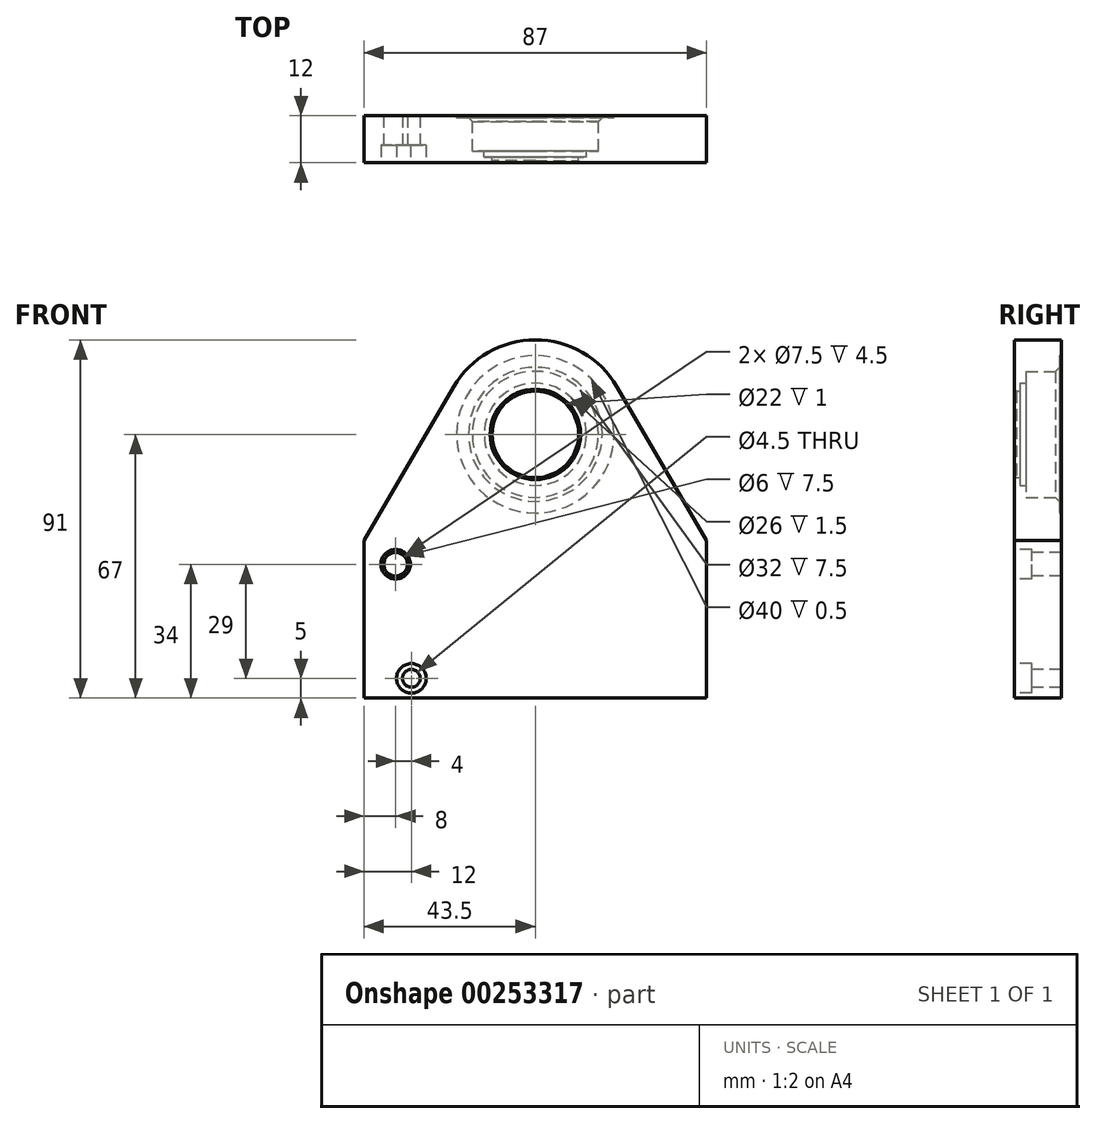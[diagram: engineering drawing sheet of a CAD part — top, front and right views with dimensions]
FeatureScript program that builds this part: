
annotation { "Feature Type Name" : "Feature", "Feature Type Description" : "" }
export const myFeature = defineFeature(function(context is Context, id is Id, definition is map)
    precondition{}
    {
        {
            var Q0;
            Q0=qCreatedBy(makeId("Front.planeOp"),FACE);
            var sketch = newSketch(context, id + "F0", { "sketchPlane" : qUnion([Q0])});
            skLineSegment(sketch, "E0.bottom", {"start": v(-43.5, 0) * mm, "end": v(43.5, 0) * mm});
            skLineSegment(sketch, "E0.left", {"start": v(-43.5, 0) * mm, "end": v(-43.5, 40) * mm});
            skLineSegment(sketch, "E0.right", {"start": v(43.5, 0) * mm, "end": v(43.5, 40) * mm});
            skCircle(sketch, "E1", {"center": v(0, 67) * mm, "radius": 11 * mm});
            skLineSegment(sketch, "E2", {"start": v(-43.5, 40) * mm, "end": v(-20.74, 79.08) * mm});
            skLineSegment(sketch, "E3", {"start": v(43.5, 40) * mm, "end": v(20.74, 79.08) * mm});
            skArc(sketch, "E4", {"start": v(-20.74, 79.08) * mm, "mid": v(0, 91) * mm, "end": v(20.74, 79.08) * mm});
            skCircle(sketch, "E5", {"center": v(-35.5, 34) * mm, "radius": 3 * mm, "construction": true});
            skCircle(sketch, "E6", {"center": v(-35.5, 34) * mm, "radius": 3.75 * mm, "construction": true});
            skCircle(sketch, "E7.MirrorC", {"center": v(35.5, 34) * mm, "radius": 3.75 * mm, "construction": true});
            skCircle(sketch, "E8.MirrorC", {"center": v(35.5, 34) * mm, "radius": 3 * mm, "construction": true});
            skCircle(sketch, "E9", {"center": v(-31.5, 5) * mm, "radius": 2.25 * mm, "construction": true});
            skCircle(sketch, "E10", {"center": v(-31.5, 5) * mm, "radius": 3.75 * mm, "construction": true});
            skCircle(sketch, "E11.MirrorC", {"center": v(31.5, 5) * mm, "radius": 2.25 * mm, "construction": true});
            skCircle(sketch, "E12.MirrorC", {"center": v(31.5, 5) * mm, "radius": 3.75 * mm, "construction": true});
            skSolve(sketch);
        }
        {
            var Q0;
            Q0=makeQuery(id+"F0.imprint","IMPRINT",FACE,{"disambiguationData":[TD([[makeQuery(id+"F0.imprint","IMPRINT",EDGE,{"derivedFrom":sQuery(id+"F0.wireOp",EDGE,"E0.bottom")}),1.0]])]});
            extrude(context, id + "F1", {"entities" : qUnion([Q0]), "depth" : 12 * mm});
        }
        {
            var Q0;
            Q0=makeQuery(id+"F1.opExtrude","CAP_FACE",FACE,{"disambiguationData":[OSD([sQuery(id+"F0.wireOp",EDGE,"E0.bottom"),sQuery(id+"F0.wireOp",EDGE,"E0.left"),sQuery(id+"F0.wireOp",EDGE,"E0.right"),sQuery(id+"F0.wireOp",EDGE,"E1"),sQuery(id+"F0.wireOp",EDGE,"E2"),sQuery(id+"F0.wireOp",EDGE,"E3"),sQuery(id+"F0.wireOp",EDGE,"E4")])],"isStart":false});
            var sketch = newSketch(context, id + "F2", { "sketchPlane" : qUnion([Q0])});
            skCircle(sketch, "E13.0", {"center": v(-35.5, 34) * mm, "radius": 3.75 * mm});
            skCircle(sketch, "E14.0", {"center": v(-35.5, 34) * mm, "radius": 3 * mm});
            skCircle(sketch, "E15.0", {"center": v(-31.5, 5) * mm, "radius": 3.75 * mm});
            skCircle(sketch, "E16.0", {"center": v(-31.5, 5) * mm, "radius": 2.25 * mm});
            skSolve(sketch);
        }
        {
            var Q0;
            Q0=makeQuery(id+"F2.imprint","IMPRINT",FACE,{"disambiguationData":[TD([[makeQuery(id+"F2.imprint","IMPRINT",EDGE,{"derivedFrom":sQuery(id+"F2.wireOp",EDGE,"E14.0")}),1.0]])]});
            extrude(context, id + "F3", {"entities" : qUnion([Q0]), "operationType" : NewBodyOperationType.REMOVE, "oppositeDirection" : true, "depth" : 18 * mm});
        }
        {
            var Q0;
            Q0=makeQuery(id+"F2.imprint","IMPRINT",FACE,{"disambiguationData":[TD([[makeQuery(id+"F2.imprint","IMPRINT",EDGE,{"derivedFrom":sQuery(id+"F2.wireOp",EDGE,"E13.0")}),1.0]])]});
            extrude(context, id + "F4", {"entities" : qUnion([Q0]), "operationType" : NewBodyOperationType.REMOVE, "oppositeDirection" : true, "depth" : 4.5 * mm});
        }
        {
            var Q0;
            Q0=makeQuery(id+"F2.imprint","IMPRINT",FACE,{"disambiguationData":[TD([[makeQuery(id+"F2.imprint","IMPRINT",EDGE,{"derivedFrom":sQuery(id+"F2.wireOp",EDGE,"E16.0")}),1.0]])]});
            extrude(context, id + "F5", {"entities" : qUnion([Q0]), "operationType" : NewBodyOperationType.REMOVE, "endBound" : BoundingType.THROUGH_ALL, "oppositeDirection" : true, "depth" : 25 * mm});
        }
        {
            var Q0;
            Q0=makeQuery(id+"F2.imprint","IMPRINT",FACE,{"disambiguationData":[TD([[makeQuery(id+"F2.imprint","IMPRINT",EDGE,{"derivedFrom":sQuery(id+"F2.wireOp",EDGE,"E15.0")}),1.0]])]});
            extrude(context, id + "F6", {"entities" : qUnion([Q0]), "operationType" : NewBodyOperationType.REMOVE, "oppositeDirection" : true, "depth" : 4.5 * mm});
        }
        {
            var Q0;
            Q0=qCreatedBy(makeId("Top.planeOp"),FACE);
            cPlane(context, id + "F7", {"entities" : qUnion([Q0]), "cplaneType" : CPlaneType.OFFSET, "offset" : 67 * mm, "width" : 150 * mm, "height" : 150 * mm});
        }
        {
            var Q0;
            Q0=qCreatedBy(id+"F7.planeOp",FACE);
            var sketch = newSketch(context, id + "F8", { "sketchPlane" : qUnion([Q0])});
            skLineSegment(sketch, "E17.0", {"start": v(-11, -12) * mm, "end": v(11, -12) * mm});
            skLineSegment(sketch, "E18.0", {"start": v(-20, 0) * mm, "end": v(20, 0) * mm});
            skLineSegment(sketch, "E19.0", {"start": v(11, -12) * mm, "end": v(-11, -12) * mm});
            skLineSegment(sketch, "E20", {"start": v(11, -12) * mm, "end": v(11, -10.5) * mm});
            skLineSegment(sketch, "E21", {"start": v(11, -10.5) * mm, "end": v(13, -10.5) * mm});
            skLineSegment(sketch, "E22", {"start": v(13, -10.5) * mm, "end": v(13, -9) * mm});
            skLineSegment(sketch, "E23", {"start": v(13, -9) * mm, "end": v(16, -9) * mm});
            skLineSegment(sketch, "E24", {"start": v(16, -9) * mm, "end": v(16, -1.5) * mm});
            skLineSegment(sketch, "E25", {"start": v(17, -0.5) * mm, "end": v(20, -0.5) * mm});
            skLineSegment(sketch, "E26", {"start": v(20, -0.5) * mm, "end": v(20, 0) * mm});
            skLineSegment(sketch, "E27", {"start": v(16, -1.5) * mm, "end": v(17, -0.5) * mm});
            skLineSegment(sketch, "E28.MirrorCS", {"start": v(-11, -12) * mm, "end": v(-11, -10.5) * mm, "construction": true});
            skLineSegment(sketch, "E29.MirrorCS", {"start": v(-13, -10.5) * mm, "end": v(-13, -9) * mm, "construction": true});
            skLineSegment(sketch, "E30.MirrorCS", {"start": v(-11, -10.5) * mm, "end": v(-13, -10.5) * mm, "construction": true});
            skLineSegment(sketch, "E31.MirrorCS", {"start": v(-13, -9) * mm, "end": v(-16, -9) * mm, "construction": true});
            skLineSegment(sketch, "E32.MirrorCS", {"start": v(-16, -9) * mm, "end": v(-16, -1.5) * mm, "construction": true});
            skLineSegment(sketch, "E33.MirrorCS", {"start": v(-17, -0.5) * mm, "end": v(-20, -0.5) * mm, "construction": true});
            skLineSegment(sketch, "E34.MirrorCS", {"start": v(-16, -1.5) * mm, "end": v(-17, -0.5) * mm, "construction": true});
            skLineSegment(sketch, "E35.MirrorCS", {"start": v(-20, -0.5) * mm, "end": v(-20, 0) * mm, "construction": true});
            skLineSegment(sketch, "E36", {"start": v(0, -26.61) * mm, "end": v(0, 7.45) * mm});
            skPoint(sketch, "E37.orphan", {"position": v(-43.5, -12) * mm});
            skPoint(sketch, "E38.orphan", {"position": v(-43.5, 0) * mm});
            skPoint(sketch, "E39.orphan", {"position": v(43.5, 0) * mm});
            skPoint(sketch, "E40.orphan", {"position": v(43.5, -12) * mm});
            skSolve(sketch);
        }
        {
            var Q0;
            Q0 = qSketchRegion(id + "F8", true);
            var Q1;
            Q1=sQuery(id+"F8.wireOp",EDGE,"E36");
            revolve(context, id + "F9", {"operationType" : NewBodyOperationType.REMOVE, "entities" : qUnion([Q0]), "axis" : qUnion([Q1]), "revolveType" : RevolveType.FULL, "oppositeDirection" : true});
        }
        {
            var Q0;
            Q0=makeQuery(id+"F1.opExtrude","CAP_EDGE",EDGE,{"disambiguationData":[OSD([sQuery(id+"F0.wireOp",EDGE,"E1")])],"isStart":false});
            chamfer(context, id + "F10", {"entities" : qUnion([Q0]), "width" : .5 * mm, "tangentPropagation" : true});
        }
    });
